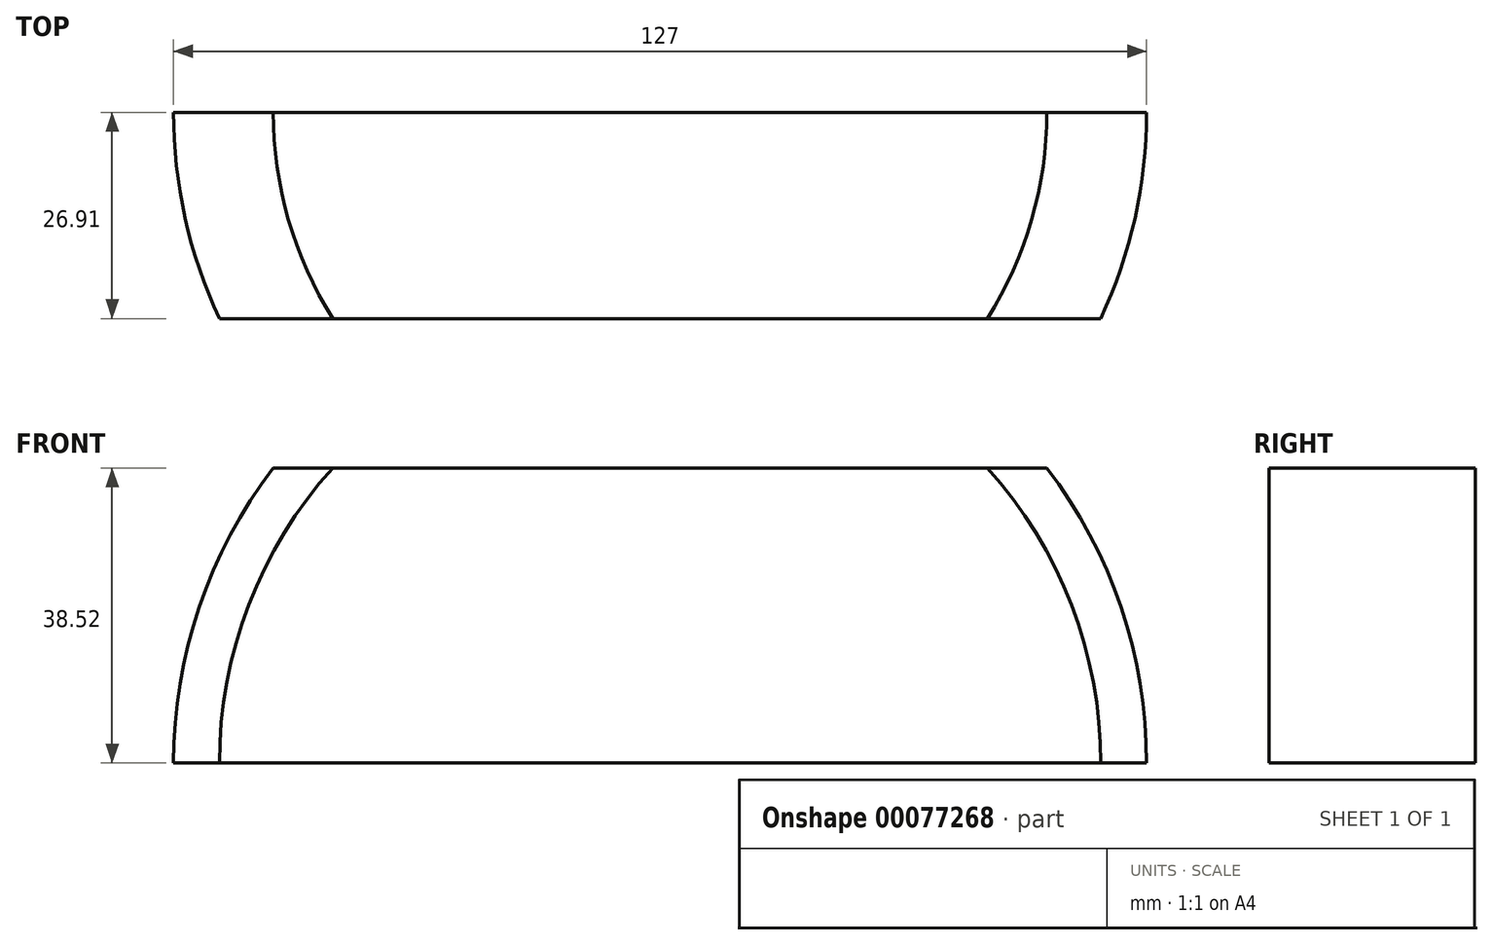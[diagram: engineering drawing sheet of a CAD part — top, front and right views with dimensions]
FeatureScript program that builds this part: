
annotation { "Feature Type Name" : "Feature", "Feature Type Description" : "" }
export const myFeature = defineFeature(function(context is Context, id is Id, definition is map)
    precondition{}
    {
        {
            var Q0;
            Q0=qCreatedBy(makeId("Right.planeOp"),FACE);
            var sketch = newSketch(context, id + "F0", { "sketchPlane" : qUnion([Q0])});
            skCircle(sketch, "E0", {"center": v(0, 0) * mm, "radius": 63.5 * mm});
            skSolve(sketch);
        }
        {
            var Q0;
            Q0 = qSketchRegion(id + "F0", true);
            extrude(context, id + "F1", {"entities" : qUnion([Q0]), "depth" : 127 * mm});
        }
        {
            var Q0;
            Q0=makeQuery(id+"F1.opExtrude","CAP_EDGE",EDGE,{"disambiguationData":[OSD([sQuery(id+"F0.wireOp",EDGE,"E0")])],"isStart":true});
            var Q1;
            Q1=makeQuery(id+"F1.opExtrude","CAP_EDGE",EDGE,{"disambiguationData":[OSD([sQuery(id+"F0.wireOp",EDGE,"E0")])],"isStart":false});
            fillet(context, id + "F2", {"entities" : qUnion([Q0, Q1]), "radius" : 63.5 * mm, "tangentPropagation" : true, "allowEdgeOverflow" : false});
        }
        {
            var Q0;
            Q0=qCreatedBy(makeId("Right.planeOp"),FACE);
            var sketch = newSketch(context, id + "F3", { "sketchPlane" : qUnion([Q0])});
            skLineSegment(sketch, "E1.bottom", {"start": v(0, 0) * mm, "end": v(-26.9, 0) * mm});
            skLineSegment(sketch, "E1.top", {"start": v(0, 38.52) * mm, "end": v(-26.9, 38.52) * mm});
            skLineSegment(sketch, "E1.left", {"start": v(0, 0) * mm, "end": v(0, 38.52) * mm});
            skLineSegment(sketch, "E1.right", {"start": v(-26.9, 0) * mm, "end": v(-26.9, 38.52) * mm});
            skSolve(sketch);
        }
        {
            var Q0;
            Q0 = qSketchRegion(id + "F3", true);
            extrude(context, id + "F4", {"entities" : qUnion([Q0]), "operationType" : NewBodyOperationType.REMOVE, "depth" : 353.52 * mm});
        }
    });
